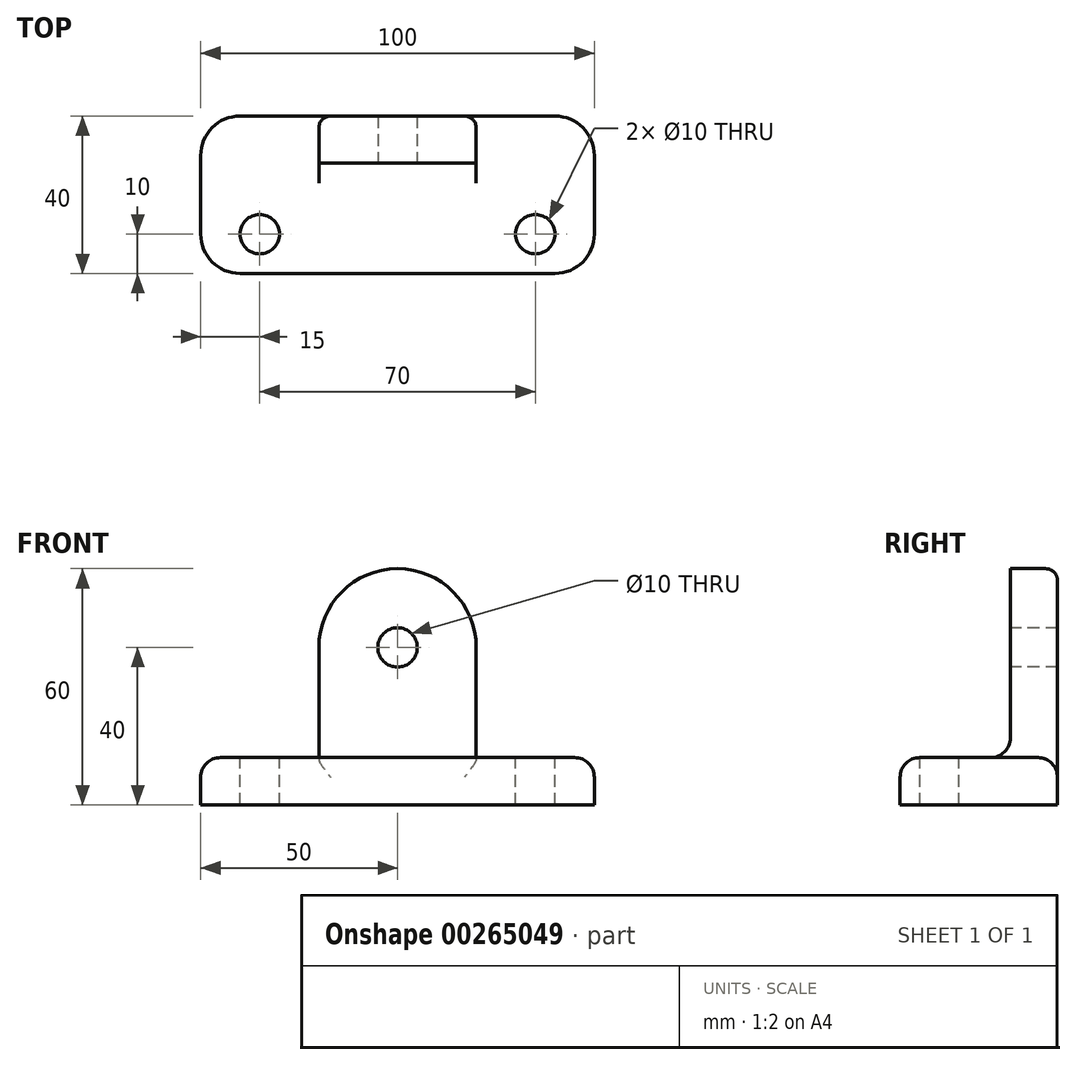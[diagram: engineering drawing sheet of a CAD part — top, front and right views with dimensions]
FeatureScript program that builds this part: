
annotation { "Feature Type Name" : "Feature", "Feature Type Description" : "" }
export const myFeature = defineFeature(function(context is Context, id is Id, definition is map)
    precondition{}
    {
        {
            var Q0;
            Q0=qCreatedBy(makeId("Top.planeOp"),FACE);
            var sketch = newSketch(context, id + "F0", { "sketchPlane" : qUnion([Q0])});
            skLineSegment(sketch, "E0.bottom", {"start": v(40, -20) * mm, "end": v(-40, -20) * mm});
            skLineSegment(sketch, "E0.top", {"start": v(40, 20) * mm, "end": v(-40, 20) * mm});
            skLineSegment(sketch, "E0.left", {"start": v(50, -10) * mm, "end": v(50, 10) * mm});
            skLineSegment(sketch, "E0.right", {"start": v(-50, -10) * mm, "end": v(-50, 10) * mm});
            skPoint(sketch, "E0.middle", {"position": v(0, 0) * mm});
            skPoint(sketch, "E1.visualSharp", {"position": v(-50, 20) * mm});
            skArc(sketch, "E1.filletArc", {"start": v(-40, 20) * mm, "mid": v(-47.07, 17.07) * mm, "end": v(-50, 10) * mm});
            skPoint(sketch, "E2.visualSharp", {"position": v(-50, -20) * mm});
            skArc(sketch, "E2.filletArc", {"start": v(-50, -10) * mm, "mid": v(-47.07, -17.07) * mm, "end": v(-40, -20) * mm});
            skPoint(sketch, "E3.visualSharp", {"position": v(50, -20) * mm});
            skArc(sketch, "E3.filletArc", {"start": v(40, -20) * mm, "mid": v(47.07, -17.07) * mm, "end": v(50, -10) * mm});
            skPoint(sketch, "E4.visualSharp", {"position": v(50, 20) * mm});
            skArc(sketch, "E4.filletArc", {"start": v(50, 10) * mm, "mid": v(47.07, 17.07) * mm, "end": v(40, 20) * mm});
            skSolve(sketch);
        }
        {
            var Q0;
            Q0 = qSketchRegion(id + "F0", true);
            extrude(context, id + "F1", {"entities" : qUnion([Q0]), "depth" : 12 * mm});
        }
        {
            var Q0;
            Q0=makeQuery(id+"F1.opExtrude","CAP_EDGE",EDGE,{"disambiguationData":[OSD([sQuery(id+"F0.wireOp",EDGE,"E0.bottom")])],"isStart":false});
            fillet(context, id + "F2", {"entities" : qUnion([Q0]), "radius" : 5 * mm, "tangentPropagation" : true, "allowEdgeOverflow" : false});
        }
        {
            var Q0;
            Q0=makeQuery(id+"F1.opExtrude","CAP_FACE",FACE,{"disambiguationData":[OSD([sQuery(id+"F0.wireOp",EDGE,"E0.bottom"),sQuery(id+"F0.wireOp",EDGE,"E0.top"),sQuery(id+"F0.wireOp",EDGE,"E0.left"),sQuery(id+"F0.wireOp",EDGE,"E0.right"),sQuery(id+"F0.wireOp",EDGE,"E1.filletArc"),sQuery(id+"F0.wireOp",EDGE,"E2.filletArc"),sQuery(id+"F0.wireOp",EDGE,"E3.filletArc"),sQuery(id+"F0.wireOp",EDGE,"E4.filletArc")])],"isStart":false});
            var sketch = newSketch(context, id + "F3", { "sketchPlane" : qUnion([Q0])});
            skCircle(sketch, "E5", {"center": v(-35, -10) * mm, "radius": 5 * mm});
            skSolve(sketch);
        }
        {
            var Q0;
            Q0 = qSketchRegion(id + "F3", true);
            extrude(context, id + "F4", {"entities" : qUnion([Q0]), "operationType" : NewBodyOperationType.REMOVE, "endBound" : BoundingType.THROUGH_ALL, "oppositeDirection" : true, "depth" : 25 * mm});
        }
        {
            var Q0;
            Q0=makeQuery(id+"F1.opExtrude","CAP_FACE",FACE,{"disambiguationData":[OSD([sQuery(id+"F0.wireOp",EDGE,"E0.bottom"),sQuery(id+"F0.wireOp",EDGE,"E0.top"),sQuery(id+"F0.wireOp",EDGE,"E0.left"),sQuery(id+"F0.wireOp",EDGE,"E0.right"),sQuery(id+"F0.wireOp",EDGE,"E1.filletArc"),sQuery(id+"F0.wireOp",EDGE,"E2.filletArc"),sQuery(id+"F0.wireOp",EDGE,"E3.filletArc"),sQuery(id+"F0.wireOp",EDGE,"E4.filletArc")])],"isStart":false});
            var sketch = newSketch(context, id + "F5", { "sketchPlane" : qUnion([Q0])});
            skCircle(sketch, "E6", {"center": v(35, -10) * mm, "radius": 5 * mm});
            skSolve(sketch);
        }
        {
            var Q0;
            Q0 = qSketchRegion(id + "F5", true);
            extrude(context, id + "F6", {"entities" : qUnion([Q0]), "operationType" : NewBodyOperationType.REMOVE, "endBound" : BoundingType.THROUGH_ALL, "oppositeDirection" : true, "depth" : 25 * mm});
        }
        {
            var Q0;
            Q0=makeQuery(id+"F1.opExtrude","CAP_FACE",FACE,{"disambiguationData":[OSD([sQuery(id+"F0.wireOp",EDGE,"E0.bottom"),sQuery(id+"F0.wireOp",EDGE,"E0.top"),sQuery(id+"F0.wireOp",EDGE,"E0.left"),sQuery(id+"F0.wireOp",EDGE,"E0.right"),sQuery(id+"F0.wireOp",EDGE,"E1.filletArc"),sQuery(id+"F0.wireOp",EDGE,"E2.filletArc"),sQuery(id+"F0.wireOp",EDGE,"E3.filletArc"),sQuery(id+"F0.wireOp",EDGE,"E4.filletArc")])],"isStart":true});
            var sketch = newSketch(context, id + "F7", { "sketchPlane" : qUnion([Q0])});
            skLineSegment(sketch, "E7.bottom", {"start": v(-20, -8) * mm, "end": v(20, -8) * mm});
            skLineSegment(sketch, "E7.top", {"start": v(-20, -20) * mm, "end": v(20, -20) * mm});
            skLineSegment(sketch, "E7.left", {"start": v(-20, -8) * mm, "end": v(-20, -20) * mm});
            skLineSegment(sketch, "E7.right", {"start": v(20, -8) * mm, "end": v(20, -20) * mm});
            skSolve(sketch);
        }
        {
            var Q0;
            Q0 = qSketchRegion(id + "F7", true);
            extrude(context, id + "F8", {"entities" : qUnion([Q0]), "operationType" : NewBodyOperationType.ADD, "oppositeDirection" : true, "depth" : 60 * mm});
        }
        {
            var Q0;
            Q0=makeQuery(id+"F8.opExtrude","SWEPT_FACE",FACE,{"disambiguationData":[OSD([sQuery(id+"F7.wireOp",EDGE,"E7.bottom")])]});
            var sketch = newSketch(context, id + "F9", { "sketchPlane" : qUnion([Q0])});
            skArc(sketch, "E8", {"start": v(20, 40) * mm, "mid": v(0, 60) * mm, "end": v(-20, 40) * mm});
            skLineSegment(sketch, "E9", {"start": v(-35.63, 47.19) * mm, "end": v(-20, 70.07) * mm});
            skLineSegment(sketch, "E10", {"start": v(-20, 70.07) * mm, "end": v(16.47, 70.07) * mm});
            skLineSegment(sketch, "E11", {"start": v(16.47, 70.07) * mm, "end": v(44.91, 67.37) * mm});
            skLineSegment(sketch, "E12", {"start": v(44.91, 67.37) * mm, "end": v(31.14, 40) * mm});
            skLineSegment(sketch, "E13", {"start": v(31.14, 40) * mm, "end": v(20, 40) * mm});
            skLineSegment(sketch, "E14", {"start": v(-20, 40) * mm, "end": v(-35.63, 47.19) * mm});
            skSolve(sketch);
        }
        {
            var Q0;
            Q0 = qSketchRegion(id + "F9", true);
            extrude(context, id + "F10", {"entities" : qUnion([Q0]), "operationType" : NewBodyOperationType.REMOVE, "oppositeDirection" : true, "depth" : 25 * mm});
        }
        {
            var Q0;
            Q0=makeQuery(id+"F10.boolean.opBoolean","COPY",EDGE,{"derivedFrom":makeQuery(id+"F10.opExtrude","CAP_EDGE",EDGE,{"disambiguationData":[OSD([sQuery(id+"F9.wireOp",EDGE,"E8")])],"isStart":true})});
            var Q1;
            Q1=makeQuery(id+"F8.opExtrude","SWEPT_EDGE",EDGE,{"disambiguationData":[OSD([sQuery(id+"F0.wireOp",EDGE,"E0.top"),sQuery(id+"F7.wireOp",EDGE,"E7.top"),sQuery(id+"F7.wireOp",EDGE,"E7.left")])]});
            fillet(context, id + "F11", {"entities" : qUnion([Q0, Q1]), "radius" : 3 * mm, "tangentPropagation" : true, "allowEdgeOverflow" : false});
        }
        {
            var Q0;
            Q0=makeQuery(id+"F8.opExtrude","SWEPT_FACE",FACE,{"disambiguationData":[OSD([sQuery(id+"F7.wireOp",EDGE,"E7.bottom")])]});
            var sketch = newSketch(context, id + "F12", { "sketchPlane" : qUnion([Q0])});
            skCircle(sketch, "E15", {"center": v(0, 40) * mm, "radius": 5 * mm});
            skSolve(sketch);
        }
        {
            var Q0;
            Q0 = qSketchRegion(id + "F12", true);
            extrude(context, id + "F13", {"entities" : qUnion([Q0]), "operationType" : NewBodyOperationType.REMOVE, "endBound" : BoundingType.THROUGH_ALL, "oppositeDirection" : true, "depth" : 25 * mm});
        }
        {
            var Q0;
            Q0=makeQuery(id+"F8.boolean.opBoolean","INTERSECT",EDGE,{"derivedFrom":[makeQuery(id+"F1.opExtrude","CAP_FACE",FACE,{"disambiguationData":[OSD([sQuery(id+"F0.wireOp",EDGE,"E0.bottom"),sQuery(id+"F0.wireOp",EDGE,"E0.top"),sQuery(id+"F0.wireOp",EDGE,"E0.left"),sQuery(id+"F0.wireOp",EDGE,"E0.right"),sQuery(id+"F0.wireOp",EDGE,"E1.filletArc"),sQuery(id+"F0.wireOp",EDGE,"E2.filletArc"),sQuery(id+"F0.wireOp",EDGE,"E3.filletArc"),sQuery(id+"F0.wireOp",EDGE,"E4.filletArc")])],"isStart":false}),makeQuery(id+"F8.opExtrude","SWEPT_FACE",FACE,{"disambiguationData":[OSD([sQuery(id+"F7.wireOp",EDGE,"E7.bottom")])]})]});
            fillet(context, id + "F14", {"entities" : qUnion([Q0]), "radius" : 5 * mm, "tangentPropagation" : true, "allowEdgeOverflow" : false});
        }
    });
